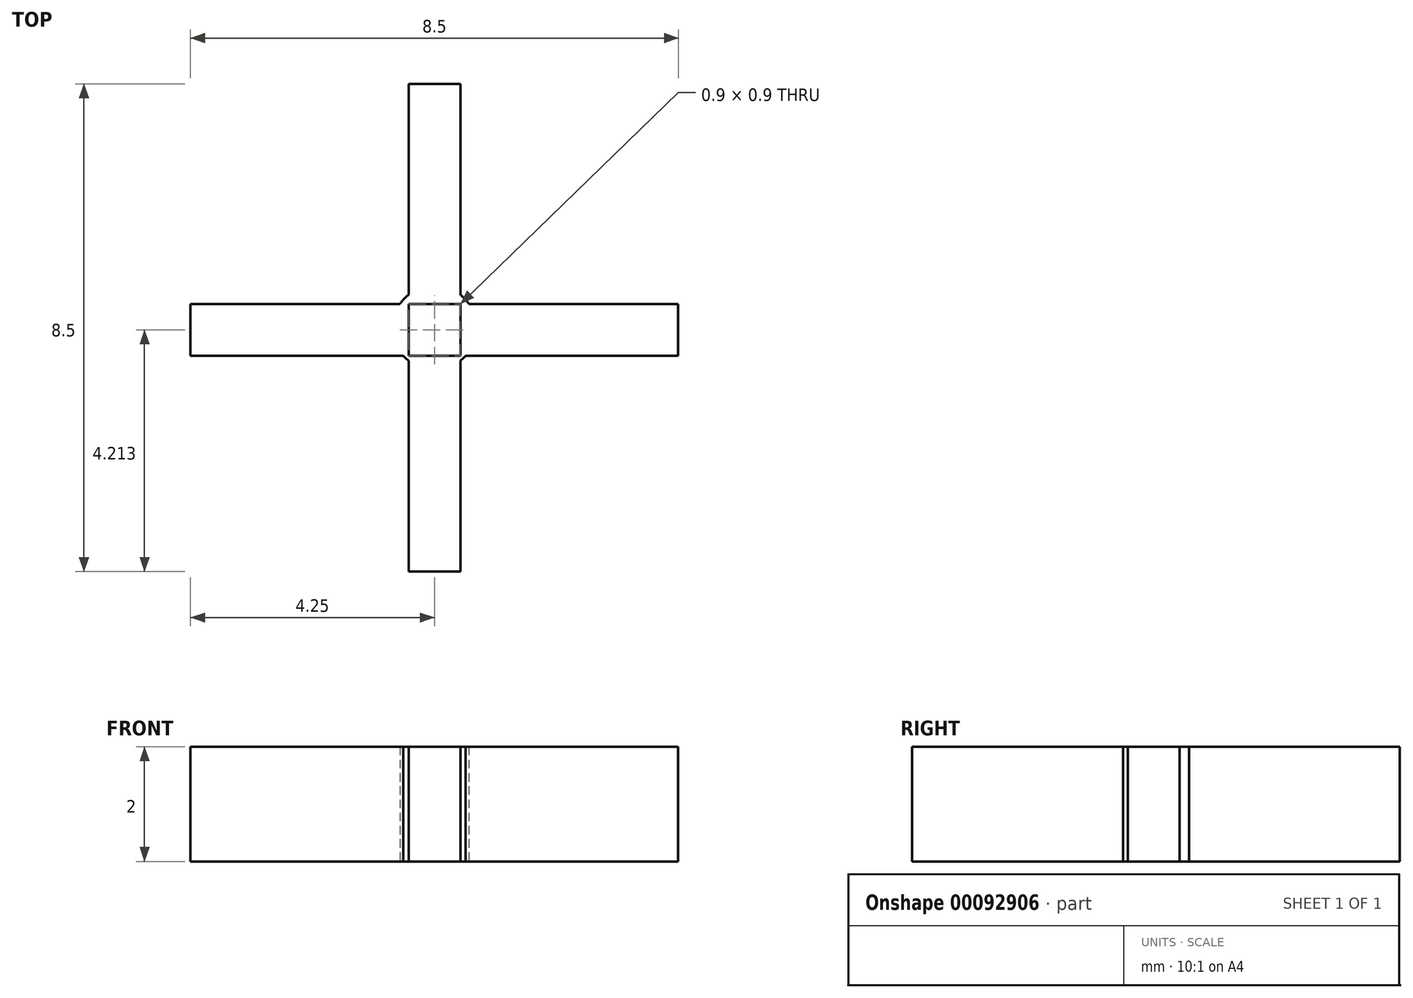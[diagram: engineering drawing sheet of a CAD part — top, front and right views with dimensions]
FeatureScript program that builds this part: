
annotation { "Feature Type Name" : "Feature", "Feature Type Description" : "" }
export const myFeature = defineFeature(function(context is Context, id is Id, definition is map)
    precondition{}
    {
        {
            var Q0;
            Q0=qCreatedBy(makeId("Top.planeOp"),FACE);
            var sketch = newSketch(context, id + "F0", { "sketchPlane" : qUnion([Q0])});
            skCircle(sketch, "E0", {"center": v(0, 0) * mm, "radius": 4.27 * mm, "construction": true});
            skCircle(sketch, "E1", {"center": v(0, 0) * mm, "radius": 0.73 * mm});
            skLineSegment(sketch, "E2.bottom", {"start": v(-4.25, 0.41) * mm, "end": v(4.25, 0.41) * mm});
            skLineSegment(sketch, "E2.top", {"start": v(-4.25, -0.49) * mm, "end": v(4.25, -0.49) * mm});
            skLineSegment(sketch, "E2.left", {"start": v(-4.25, 0.41) * mm, "end": v(-4.25, -0.49) * mm});
            skLineSegment(sketch, "E2.right", {"start": v(4.25, 0.41) * mm, "end": v(4.25, -0.49) * mm});
            skLineSegment(sketch, "E3.bottom", {"start": v(0.45, 4.25) * mm, "end": v(-0.45, 4.25) * mm});
            skLineSegment(sketch, "E3.top", {"start": v(0.45, -4.25) * mm, "end": v(-0.45, -4.25) * mm});
            skLineSegment(sketch, "E3.left", {"start": v(0.45, 4.25) * mm, "end": v(0.45, -4.25) * mm});
            skLineSegment(sketch, "E3.right", {"start": v(-0.45, 4.25) * mm, "end": v(-0.45, -4.25) * mm});
            skSolve(sketch);
        }
        {
            var Q0;
            Q0 = qSketchRegion(id + "F0", true);
            extrude(context, id + "F1", {"entities" : qUnion([Q0]), "depth" : 2 * mm});
        }
        {
            var Q0;
            Q0=sQuery(id+"F0.wireOp",EDGE,"E1");
            extrude(context, id + "F2", {"bodyType" : ToolBodyType.SURFACE, "surfaceEntities" : qUnion([Q0]), "depth" : 3 * mm});
        }
    });
